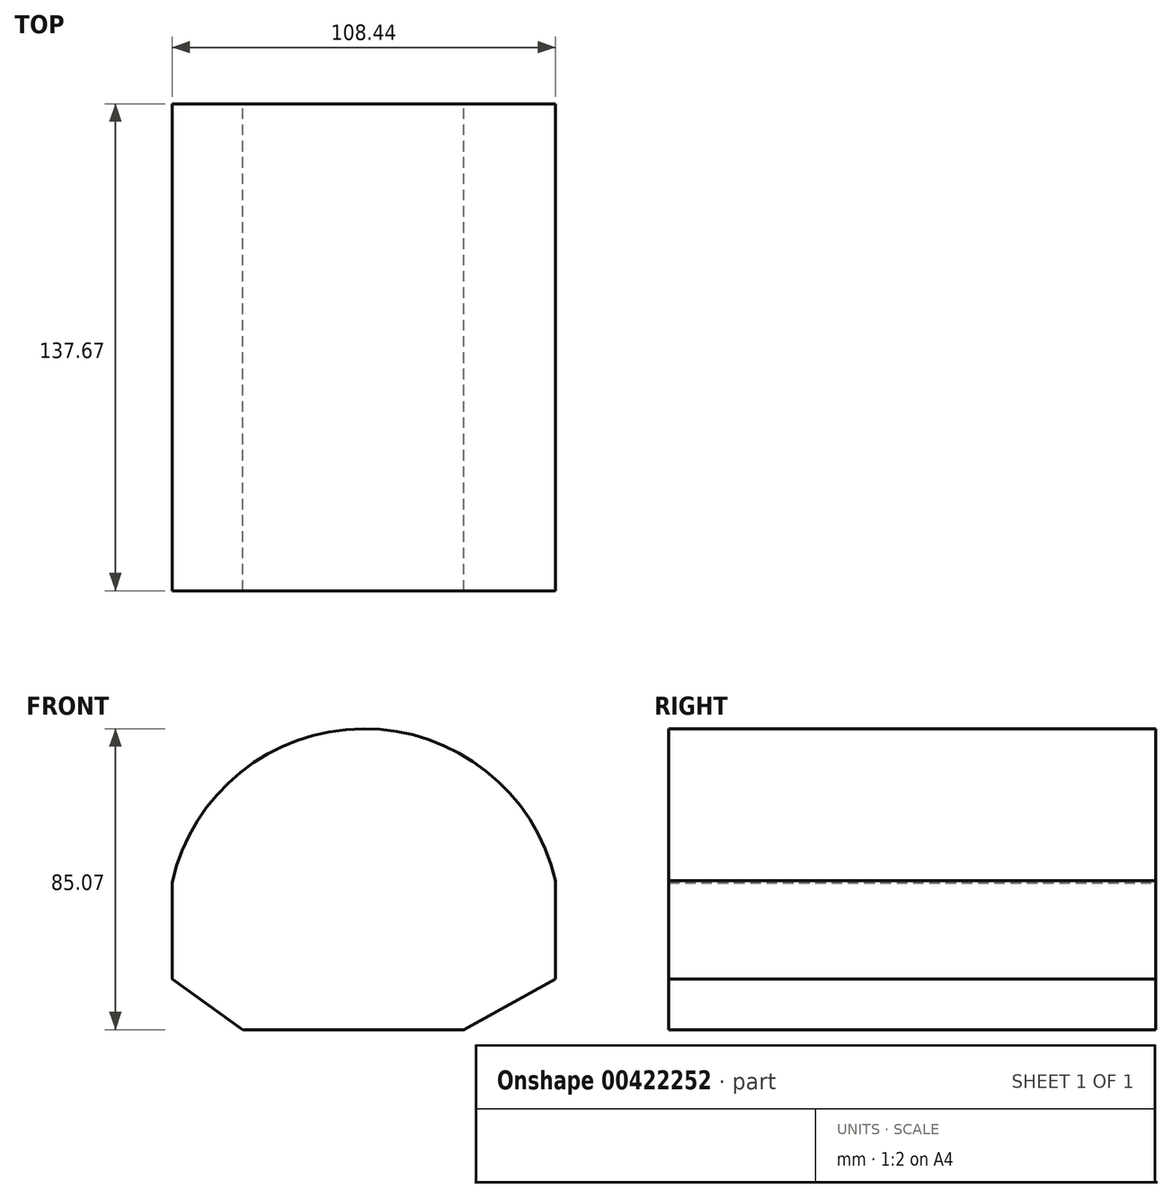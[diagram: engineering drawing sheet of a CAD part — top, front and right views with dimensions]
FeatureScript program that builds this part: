
annotation { "Feature Type Name" : "Feature", "Feature Type Description" : "" }
export const myFeature = defineFeature(function(context is Context, id is Id, definition is map)
    precondition{}
    {
        {
            var Q0;
            Q0=qCreatedBy(makeId("Front.planeOp"),FACE);
            var sketch = newSketch(context, id + "F0", { "sketchPlane" : qUnion([Q0])});
            skArc(sketch, "E0", {"start": v(51.49, 27.82) * mm, "mid": v(-2.97, 70.8) * mm, "end": v(-56.95, 27.2) * mm});
            skLineSegment(sketch, "E1", {"start": v(-56.95, 27.2) * mm, "end": v(-56.95, 0) * mm});
            skLineSegment(sketch, "E2", {"start": v(-56.95, 0) * mm, "end": v(-36.92, -14.26) * mm});
            skLineSegment(sketch, "E3", {"start": v(51.49, 27.82) * mm, "end": v(51.49, 0) * mm});
            skLineSegment(sketch, "E4", {"start": v(-36.92, -14.26) * mm, "end": v(25.6, -14.26) * mm});
            skLineSegment(sketch, "E5", {"start": v(25.6, -14.26) * mm, "end": v(51.49, 0) * mm});
            skSolve(sketch);
        }
        {
            var Q0;
            Q0=makeQuery(id+"F0.imprint","IMPRINT",FACE,{"disambiguationData":[TD([[makeQuery(id+"F0.imprint","IMPRINT",EDGE,{"derivedFrom":sQuery(id+"F0.wireOp",EDGE,"E0")}),1.0]])]});
            extrude(context, id + "F1", {"entities" : qUnion([Q0]), "depth" : 137.67 * mm, "offsetDistance" : 25.4 * mm});
        }
    });
